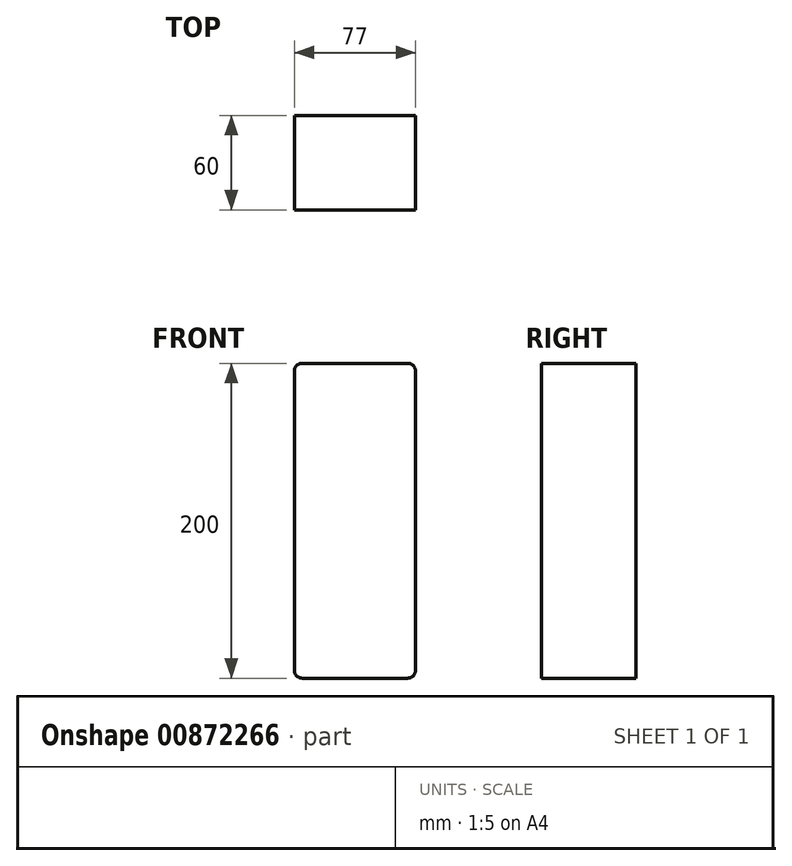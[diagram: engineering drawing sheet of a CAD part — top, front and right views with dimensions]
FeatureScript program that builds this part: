
annotation { "Feature Type Name" : "Feature", "Feature Type Description" : "" }
export const myFeature = defineFeature(function(context is Context, id is Id, definition is map)
    precondition{}
    {
        {
            var Q0;
            Q0=qCreatedBy(makeId("Front.planeOp"),FACE);
            var sketch = newSketch(context, id + "F0", { "sketchPlane" : qUnion([Q0])});
            skLineSegment(sketch, "E0.bottom", {"start": v(33.5, -100) * mm, "end": v(-33.5, -100) * mm});
            skLineSegment(sketch, "E0.top", {"start": v(33.5, 100) * mm, "end": v(-33.5, 100) * mm});
            skLineSegment(sketch, "E0.left", {"start": v(38.5, -95) * mm, "end": v(38.5, 95) * mm});
            skLineSegment(sketch, "E0.right", {"start": v(-38.5, -95) * mm, "end": v(-38.5, 95) * mm});
            skPoint(sketch, "E0.middle", {"position": v(0, 0) * mm});
            skPoint(sketch, "E1.visualSharp", {"position": v(-38.5, 100) * mm});
            skArc(sketch, "E1.filletArc", {"start": v(-33.5, 100) * mm, "mid": v(-37.04, 98.54) * mm, "end": v(-38.5, 95) * mm});
            skPoint(sketch, "E2.visualSharp", {"position": v(38.5, 100) * mm});
            skArc(sketch, "E2.filletArc", {"start": v(38.5, 95) * mm, "mid": v(37.04, 98.54) * mm, "end": v(33.5, 100) * mm});
            skPoint(sketch, "E3.visualSharp", {"position": v(-38.5, -100) * mm});
            skArc(sketch, "E3.filletArc", {"start": v(-38.5, -95) * mm, "mid": v(-37.04, -98.54) * mm, "end": v(-33.5, -100) * mm});
            skPoint(sketch, "E4.visualSharp", {"position": v(38.5, -100) * mm});
            skArc(sketch, "E4.filletArc", {"start": v(33.5, -100) * mm, "mid": v(37.04, -98.54) * mm, "end": v(38.5, -95) * mm});
            skSolve(sketch);
        }
        {
            var Q0;
            Q0=makeQuery(id+"F0.imprint","IMPRINT",FACE,{"disambiguationData":[TD([[makeQuery(id+"F0.imprint","IMPRINT",EDGE,{"derivedFrom":sQuery(id+"F0.wireOp",EDGE,"E0.bottom")}),-1.0]])]});
            extrude(context, id + "F1", {"entities" : qUnion([Q0]), "endBound" : BoundingType.SYMMETRIC, "depth" : 60 * mm, "offsetDistance" : 25 * mm});
        }
    });
